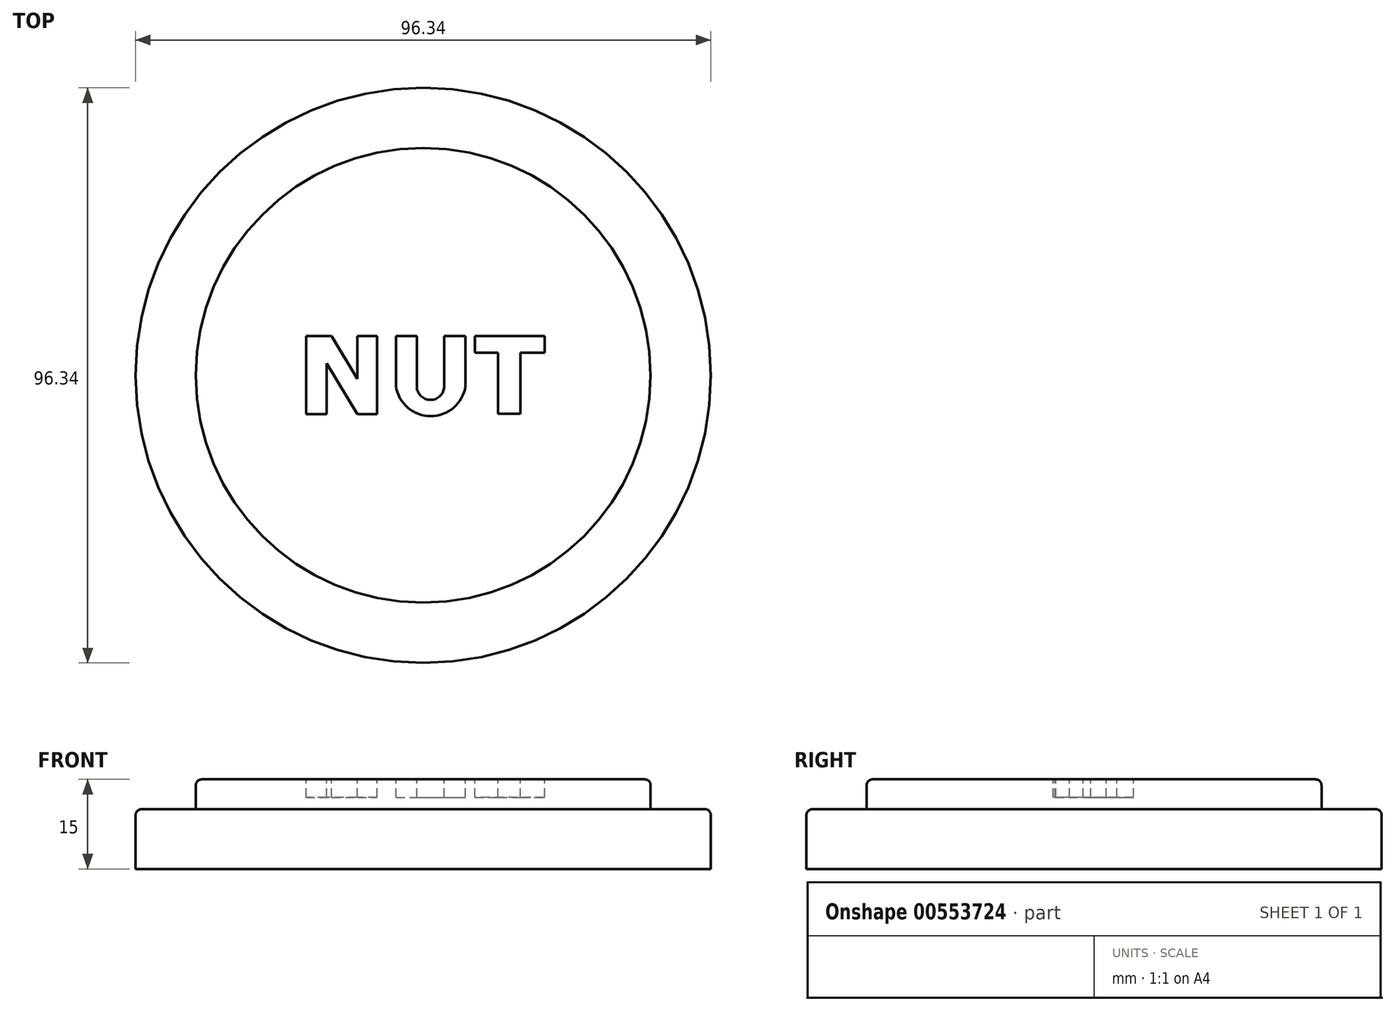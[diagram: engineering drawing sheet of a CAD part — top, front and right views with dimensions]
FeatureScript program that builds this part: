
annotation { "Feature Type Name" : "Feature", "Feature Type Description" : "" }
export const myFeature = defineFeature(function(context is Context, id is Id, definition is map)
    precondition{}
    {
        {
            var Q0;
            Q0=qCreatedBy(makeId("Top.planeOp"),FACE);
            var sketch = newSketch(context, id + "F0", { "sketchPlane" : qUnion([Q0])});
            skLineSegment(sketch, "E0", {"start": v(0, -38.1) * mm, "end": v(76.2, -38.1) * mm, "construction": true});
            skLineSegment(sketch, "E1", {"start": v(38.1, 0) * mm, "end": v(38.1, -76.2) * mm, "construction": true});
            skCircle(sketch, "E2", {"center": v(38.1, -38.1) * mm, "radius": 48.17 * mm});
            skSolve(sketch);
        }
        {
            var Q0;
            Q0 = qSketchRegion(id + "F0", true);
            extrude(context, id + "F1", {"entities" : qUnion([Q0]), "depth" : 10 * mm, "offsetDistance" : 25.4 * mm});
        }
        {
            var Q0;
            Q0=makeQuery(id+"F1.opExtrude","CAP_FACE",FACE,{"disambiguationData":[OSD([sQuery(id+"F0.wireOp",EDGE,"E2")])],"isStart":false});
            var sketch = newSketch(context, id + "F2", { "sketchPlane" : qUnion([Q0])});
            skCircle(sketch, "E3", {"center": v(38.1, -38.1) * mm, "radius": 38.09 * mm});
            skSolve(sketch);
        }
        {
            var Q0;
            Q0 = qSketchRegion(id + "F2", true);
            extrude(context, id + "F3", {"entities" : qUnion([Q0]), "operationType" : NewBodyOperationType.ADD, "depth" : 5 * mm, "offsetDistance" : 25.4 * mm});
        }
        {
            var Q0;
            Q0=makeQuery(id+"F3.opExtrude","CAP_FACE",FACE,{"disambiguationData":[OSD([sQuery(id+"F2.wireOp",EDGE,"E3")])],"isStart":false});
            var sketch = newSketch(context, id + "F4", { "sketchPlane" : qUnion([Q0])});
            skLineSegment(sketch, "E4", {"start": v(18.48, -31.49) * mm, "end": v(22.78, -31.49) * mm});
            skLineSegment(sketch, "E5", {"start": v(22.78, -31.49) * mm, "end": v(27.1, -38.67) * mm});
            skLineSegment(sketch, "E6", {"start": v(27.1, -38.67) * mm, "end": v(27.1, -31.49) * mm});
            skLineSegment(sketch, "E7", {"start": v(27.1, -31.49) * mm, "end": v(30.37, -31.49) * mm});
            skLineSegment(sketch, "E8", {"start": v(30.37, -31.49) * mm, "end": v(30.37, -44.62) * mm});
            skLineSegment(sketch, "E9", {"start": v(30.37, -44.62) * mm, "end": v(27.07, -44.62) * mm});
            skLineSegment(sketch, "E10", {"start": v(27.07, -44.62) * mm, "end": v(21.93, -36.08) * mm});
            skLineSegment(sketch, "E11", {"start": v(21.93, -36.08) * mm, "end": v(21.93, -44.62) * mm});
            skLineSegment(sketch, "E12", {"start": v(21.93, -44.62) * mm, "end": v(18.52, -44.62) * mm});
            skLineSegment(sketch, "E13", {"start": v(18.52, -44.62) * mm, "end": v(18.48, -31.49) * mm});
            skLineSegment(sketch, "E14", {"start": v(33.53, -31.49) * mm, "end": v(37.03, -31.49) * mm});
            skLineSegment(sketch, "E15", {"start": v(37.03, -31.49) * mm, "end": v(37.03, -39.92) * mm});
            skArc(sketch, "E16", {"start": v(37.03, -39.92) * mm, "mid": v(39.32, -42.21) * mm, "end": v(41.62, -39.92) * mm});
            skLineSegment(sketch, "E17", {"start": v(41.62, -39.92) * mm, "end": v(41.62, -31.49) * mm});
            skLineSegment(sketch, "E18", {"start": v(41.62, -31.49) * mm, "end": v(45.18, -31.49) * mm});
            skLineSegment(sketch, "E19", {"start": v(45.18, -31.49) * mm, "end": v(45.18, -39.92) * mm});
            skLineSegment(sketch, "E20", {"start": v(33.53, -31.49) * mm, "end": v(33.53, -39.92) * mm});
            skArc(sketch, "E21", {"start": v(33.53, -39.92) * mm, "mid": v(39.36, -44.94) * mm, "end": v(45.18, -39.92) * mm});
            skLineSegment(sketch, "E22", {"start": v(46.74, -31.49) * mm, "end": v(46.74, -34.3) * mm});
            skLineSegment(sketch, "E23", {"start": v(46.74, -34.3) * mm, "end": v(50.63, -34.3) * mm});
            skLineSegment(sketch, "E24", {"start": v(50.63, -34.3) * mm, "end": v(50.63, -44.53) * mm});
            skLineSegment(sketch, "E25", {"start": v(50.63, -44.53) * mm, "end": v(54.39, -44.53) * mm});
            skLineSegment(sketch, "E26", {"start": v(54.39, -44.53) * mm, "end": v(54.39, -34.3) * mm});
            skLineSegment(sketch, "E27", {"start": v(54.39, -34.3) * mm, "end": v(58.47, -34.3) * mm});
            skLineSegment(sketch, "E28", {"start": v(58.47, -34.3) * mm, "end": v(58.47, -31.49) * mm});
            skLineSegment(sketch, "E29", {"start": v(58.47, -31.49) * mm, "end": v(46.74, -31.49) * mm});
            skSolve(sketch);
        }
        {
            var Q0;
            Q0 = qSketchRegion(id + "F4", true);
            extrude(context, id + "F5", {"entities" : qUnion([Q0]), "operationType" : NewBodyOperationType.REMOVE, "oppositeDirection" : true, "depth" : 3 * mm, "offsetDistance" : 25.4 * mm});
        }
        {
            var Q0;
            Q0=makeQuery(id+"F1.opExtrude","CAP_EDGE",EDGE,{"disambiguationData":[OSD([sQuery(id+"F0.wireOp",EDGE,"E2")])],"isStart":false});
            var Q1;
            Q1=makeQuery(id+"F3.opExtrude","CAP_EDGE",EDGE,{"disambiguationData":[OSD([sQuery(id+"F2.wireOp",EDGE,"E3")])],"isStart":false});
            fillet(context, id + "F6", {"entities" : qUnion([Q0, Q1]), "tangentPropagation" : true, "radius" : 1 * mm, "defaultsChanged" : true, "vertexSettings" : [], "allowEdgeOverflow" : false});
        }
    });
